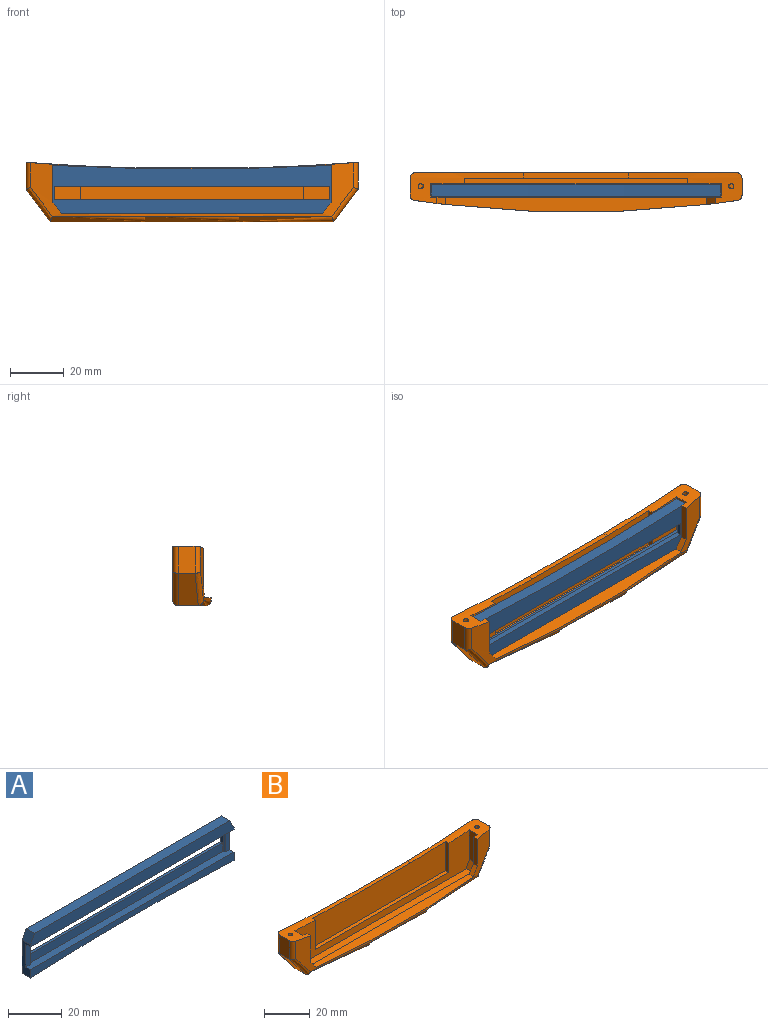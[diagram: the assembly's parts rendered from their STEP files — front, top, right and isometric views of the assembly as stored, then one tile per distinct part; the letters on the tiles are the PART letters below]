
ASSEMBLY  parts=2 mates=1
PART A: 19 faces, bbox 107.3x4.4x19.2 mm
  f0: plane 107.32x10.3mm, normal (0,-1,0), area 180.2mm2, adj f3,f5,f8,f11,f14,f16,f18
  f1: plane 102x1.2mm, normal (0,0,1), area 122.4mm2, adj f2,f7,f9,f15
  f2: plane 9x1.6mm, normal (1,0,0), area 9.6mm2, adj f1,f3,f7,f8,f9,f14
  f3: plane 102.8x2mm, normal (0,0,-1), area 204.2mm2, adj f0,f2,f7,f14,f15,f18
  f4: plane 102.92x4.4mm, normal (0,0,1), area 452.8mm2, adj f7,f12,f13,f17
  f5: plane 15x4.4mm, normal (-1,0,0), area 41.3mm2, adj f0,f6,f7,f8,f10,f11,f12,f13
  f6: cylinder r=1029.06mm len=107.32mm, axis (0,1,0), area 472.4mm2, adj f5,f7,f10,f16
  f7: plane 107.32x19.2mm, normal (0,1,0), area 1441.1mm2, adj f1,f2,f3,f4,f5,f6,f13,f15
  f8: plane 107.32x3.2mm, normal (0,0,1), area 339.3mm2, adj f0,f2,f5,f9,f10,f14,f15,f16
  f9: plane 102x4mm, normal (0,-1,0), area 408mm2, adj f1,f2,f8,f15
  f10: plane 107.32x3.8mm, normal (0,-1,0), area 307.6mm2, adj f5,f6,f8,f16
  f11: plane 107.32x2.4mm, normal (0,0,-1), area 257.6mm2, adj f0,f5,f12,f16
  f12: plane 107.32x5.1mm, normal (0,-1,0), area 538.1mm2, adj f4,f5,f11,f13,f16,f17
  f13: plane 4.4x4.2mm, normal (-0.89,0,0.46), area 20.9mm2, adj f4,f5,f7,f12
  f14: plane 9x0.4mm, normal (0.71,-0.71,0), area 5.1mm2, adj f0,f2,f3,f8
  f15: plane 9x1.6mm, normal (-1,0,0), area 9.6mm2, adj f1,f3,f7,f8,f9,f18
  f16: plane 15x4.4mm, normal (1,0,0), area 41.3mm2, adj f0,f6,f7,f8,f10,f11,f12,f17
  f17: plane 4.4x4.2mm, normal (0.89,0,0.46), area 20.9mm2, adj f4,f7,f12,f16
  f18: plane 9x0.4mm, normal (-0.71,-0.71,0), area 5.1mm2, adj f0,f3,f8,f15
PART B: 44 faces, bbox 183.2x17.9x96.8 mm
  f0: plane 39.21x2mm, normal (0,0,1), area 78.4mm2, adj f1,f15,f24,f40
  f1: plane 119x19.84mm, normal (0,1,0), area 2008.1mm2, adj f0,f6,f18,f19,f20,f24,f29,f36
  f2: plane 10x6.27mm, normal (-1,0,0), area 62.7mm2, adj f17,f19,f21,f23,f24
  f3: plane 105x10.56mm, normal (0,0,-1), area 992.3mm2, adj f17,f18,f22,f35
  f4: cylinder r=417mm len=119.57mm, axis (0,0,-1), area 356.1mm2, adj f5,f8,f21,f22,f23,f24,f25,f31
  f5: plane 97x5.56mm, normal (0,0,1), area 447.9mm2, adj f4,f11,f25,f41
  f6: cylinder r=4.1mm len=8.2mm, axis (0,1,0), area 92.7mm2, adj f1,f7
  f7: plane 8.2x8.2mm, normal (0,1,0), area 52.8mm2, adj f6
  f8: plane 14.27x2.37mm, normal (1,0,0), area 33.8mm2, adj f4,f11,f24,f25
  f9: plane 15.59x2mm, normal (1,0,0), area 31.2mm2, adj f10,f12,f15,f24
  f10: plane 82.33x2mm, normal (0,0,1), area 164.7mm2, adj f9,f12,f15,f32
  f11: plane 107.8x19.73mm, normal (0,1,0), area 232.2mm2, adj f5,f8,f13,f14,f16,f24,f25,f31
  f12: plane 107.8x19.73mm, normal (0,-1,0), area 764.7mm2, adj f9,f10,f13,f14,f16,f24,f32,f33
  f13: plane 15.73x5mm, normal (1,0,0), area 78.7mm2, adj f11,f12,f16,f24
  f14: plane 103.8x5mm, normal (0,0,1), area 519mm2, adj f11,f12,f16,f34
  f15: plane 82.33x15.59mm, normal (0,-1,0), area 1238.7mm2, adj f0,f9,f10,f24,f32,f40
  f16: plane 5x4mm, normal (0.89,0,0.45), area 22.4mm2, adj f11,f12,f13,f14
  f17: plane 12x9mm, normal (-0.8,0,-0.6), area 102.6mm2, adj f2,f3,f20,f22,f23
  f18: cylinder r=2mm len=105mm, axis (-1,0,0), area 326.7mm2, adj f1,f3,f20,f37
  f19: cylinder r=2mm len=10mm, axis (0,0,1), area 30.1mm2, adj f1,f2,f20,f24
  f20: cylinder r=2mm len=13.2mm, axis (0.6,0,-0.8), area 44.5mm2, adj f1,f17,f18,f19
  f21: cylinder r=2mm len=10mm, axis (0,0,-1), area 27.4mm2, adj f2,f4,f23,f24
  f22: torus R=415mm, axis (0,0,1), area 329.4mm2, adj f3,f4,f17,f23,f35,f39
  f23: bspline ~96.85x73.38mm, area 42.2mm2, adj f2,f4,f17,f21,f22
  f24: cylinder r=645.21mm len=41.9mm, axis (0,1,0), area 173.1mm2, adj f0,f1,f2,f4,f8,f9,f11,f12
  f25: plane 4x3mm, normal (0.8,0,0.6), area 12.8mm2, adj f4,f5,f8,f11
  f26: cylinder r=1mm len=7.06mm, axis (0.06,0,1), area 43.6mm2, adj f24,f27
  f27: plane 2x2mm, normal (0.06,0,1), area 3.1mm2, adj f26
  f28: plane 10x6.27mm, normal (1,0,0), area 62.7mm2, adj f35,f36,f38,f39,f40
  f29: cylinder r=4.1mm len=8.2mm, axis (0,1,0), area 92.7mm2, adj f1,f30
  f30: plane 8.2x8.2mm, normal (0,1,0), area 52.8mm2, adj f29
  f31: plane 14.27x2.37mm, normal (-1,0,0), area 33.8mm2, adj f4,f11,f40,f41
  f32: plane 15.59x2mm, normal (-1,0,0), area 31.2mm2, adj f10,f12,f15,f40
  f33: plane 15.73x5mm, normal (-1,0,0), area 78.7mm2, adj f11,f12,f34,f40
  f34: plane 5x4mm, normal (-0.89,0,0.45), area 22.4mm2, adj f11,f12,f14,f33
  f35: plane 12x9mm, normal (0.8,0,-0.6), area 102.6mm2, adj f3,f22,f28,f37,f39
  f36: cylinder r=2mm len=10mm, axis (0,0,1), area 30.1mm2, adj f1,f28,f37,f40
  f37: cylinder r=2mm len=13.2mm, axis (-0.6,0,-0.8), area 44.5mm2, adj f1,f18,f35,f36
  f38: cylinder r=2mm len=10mm, axis (0,0,-1), area 27.4mm2, adj f4,f28,f39,f40
  f39: bspline ~96.85x73.38mm, area 42.2mm2, adj f4,f22,f28,f35,f38
  f40: cylinder r=645.21mm len=41.9mm, axis (0,1,0), area 173.1mm2, adj f0,f1,f4,f11,f12,f15,f28,f31
  f41: plane 4x3mm, normal (-0.8,0,0.6), area 12.8mm2, adj f4,f5,f11,f31
  f42: cylinder r=1mm len=7.06mm, axis (-0.06,0,1), area 43.6mm2, adj f40,f43
  f43: plane 2x2mm, normal (-0.06,0,1), area 3.1mm2, adj f42
PLACE A rot(axis=(1,0,0),180deg) t=(0,-5.7,10.6)mm
PLACE B t=(0,-2,0)mm
MATE fastened A.f4 <-> B.f14  axis (0,0,-1) through (0,-3.5,1.7)mm
